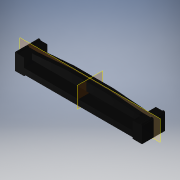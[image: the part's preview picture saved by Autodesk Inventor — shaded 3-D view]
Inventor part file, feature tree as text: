
AUTODESK INVENTOR PART (.ipt)
format: ipt  version: 2019 (Build 230136000, 136)  size: 239,104 bytes
history: native  units: mm (DEFAULTED — no unit token found)
features: sketch x8, extrude x5, fillet x1
ambient origin geometry x8: Origin, YZ Plane, XZ Plane, XY Plane, X Axis, Y Axis, Z Axis, Center Point
bodies: Solid1 (feature_tree)
feature tree (14):
  extrude  "Extrusion1"  Depth=10.0mm
  extrude  "Extrusion2"  Depth=47.0mm
  extrude  "Extrusion3"  Depth=7.4676mm TaperAngle=0.0deg
  extrude  "Extrusion4"  Depth=2.54mm
  extrude  "Extrusion5"  Depth=1.3208mm
  fillet  "Fillet1"  Radius=0.762mm
  sketch  "Sketch8"  dims[d15=8.128mm]
  sketch  "Sketch9"  dims[d16=16.891mm]
  sketch  "Sketch11"  dims[d17=0.508mm d18=3.302mm d19=0.0mm d20=1.143mm d21=3.302mm d22=0.0mm d23=0.5842mm d37=0.508mm d38=0.5842mm d39=0.254mm d40=160.0mm d42=1.27mm d43=10.0mm d45=25.4mm d48=1.27mm d49=1.27mm d50=1.27mm d51=1.27mm d53=1.27mm d54=1.27mm d55=1.27mm d56=1.27mm d57=1.27mm d58=1.27mm d59=1.27mm d60=1.27mm d61=1.27mm d62=1.27mm d64=0.4318mm d65=2.032mm d66=1.27mm d67=0.4318mm d68=0.4318mm d69=1.27mm d70=20.0mm d72=22.86mm d73=10.0mm d75=25.4mm d77=20.0mm d79=1.3843mm d80=10.0mm d82=25.4mm d84=20.0mm d86=1.016mm d87=10.0mm d89=25.4mm d91=20.0mm d93=1.016mm d94=10.0mm d96=25.4mm]
  sketch  "Sketch1"  dims[d0=55.0mm d1=10.0mm]
  sketch  "Sketch2"  dims[d2=7.4676mm d3=0.0mm d4=47.0mm]
  sketch  "Sketch3"  dims[d5=0.5842mm d6=7.4676mm d7=0.0mm]
  sketch  "Sketch4"  dims[d8=47.0mm d9=2.54mm]
  sketch  "Sketch5"  dims[d11=7.4676mm d12=0.0mm d13=1.3208mm d14=0.762mm]
